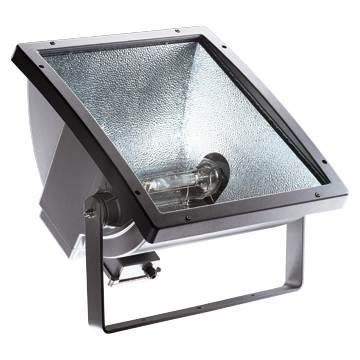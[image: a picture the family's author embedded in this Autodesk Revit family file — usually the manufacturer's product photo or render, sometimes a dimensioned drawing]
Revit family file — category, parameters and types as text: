
# Revit family: Lighting-Proiezione-GEWISS-STADIUM-PROIETTORI_OTTICA_SIMMETRICA
name_source: partatom
category: Apparecchi per illuminazione
units: mm (PartAtom-declared; Revit-internal decimal feet)

## family parameters
Condiviso = No
Host = Superficie
Numero OmniClass = 23.80.70.00
Punto di calcolo locali = Sì
Quota connettore circolare = Usa diametro
Sorgente d'illuminazione = No
Taglio con vuoti quando caricato = No
Tipo di parte = Normale
Titolo OmniClass = Lighting

## types (2) — shared parameters
Applicazione = Esterno
Attacco lampada = E40
Carico apparente = 2000 VA
Catalogo = LIGHTING
Catalogo Serie = Stadium
Classe isolamento = I
Codice Electrocod = 2433
Colore = Grigio grafite
Commenti sul wattaggio = 2000W
Cornice = GEWISS - Grigio Grafite
Corrente lampada = 10,3A
Corrente lampada: = 10,3A
Distanza minima dall'oggetto illuminato = 3M
Grado di protezione = IP66
H_Centro rotazione = 296 mm  [stored 0.971129 ft]
IDF = 73cd6bd1-190e-40e0-813a-6cfb409f80a8
IDT = e7e39371-c899-4443-9a56-f03baa1dbdb0
Immagine tipo = GW84662.jpg
Inquinamento luminoso = 0 cd/Klm
L_interna staffa = 612 mm  [stored 2.00787 ft]
Lampada = MT
Led = GEWISS - Led
Lunghezza proiettore = 604 mm  [stored 1.98163 ft]
Materiale = Alluminio
Numero di poli = 2
Ottica = Simmetrica diffondente - ULOR: 0%
Ottica- = GEWISS - Ottica
Produttore = GEWISS S.p.A.
Prospetto di default = 1219 mm
Resistenza agli urti = IK09
SEO = Proiettore
Scheda Tecnica = https://www.gewiss.com
Struttura = <Per categoria>
Superficie laterale esposta al vento = 0,141M2
Superficie massima esposta al vento = 0,392M2
URL = https://www.gewiss.com
Versione file RFA = 20.11
Vetro = GEWISS - vetro acceso
Voltaggio = 230 V

## per-type parameters (varying)
| type | Codice EAN | Descrizione | Lampada: | Modello | Peso (kg) | Peso (kg): | Potenza lampada |
| GW84663 - STADIUM SIM. DIF. 2000W MT E40 | 8011564035676 | STADIUM OTTICA SIMMETRICA DIFFONDENTE 2000W MT E40 | MT | GW84663 | 23,5 | 23,5 | 2000W |
| GW84662 - STADIUM SIM. DIF. 1000W ST E40 | 8011564035669 | STADIUM OTTICA SIMMETRICA DIFFONDENTE 1000W ST E40 | ST | GW84662 | 24,1 | 24,1 | 1000W |

note: [stored X ft] marks values corroborated as IEEE doubles in the binary element streams (Revit-internal decimal feet)

## geometry (parser evidence)
native form markers: Blend x393
no freeform markers — native parametric forms only
